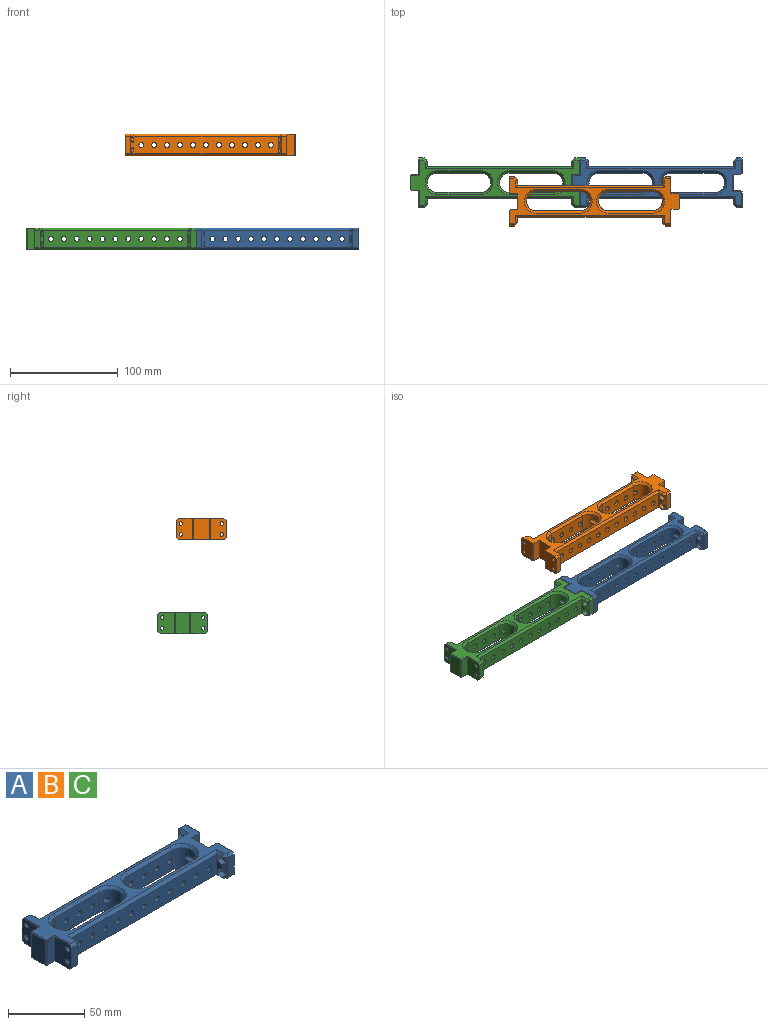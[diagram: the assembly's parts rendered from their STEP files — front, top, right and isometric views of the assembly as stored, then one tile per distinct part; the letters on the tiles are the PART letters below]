
ASSEMBLY  parts=3 mates=1
PART A: 168 faces, bbox 158.1x46.1x20.1 mm
  f0: plane 16x5mm, normal (1,0,0), area 39.9mm2, adj f20,f83,f84,f106,f142,f149
  f1: plane 0.54x0.14mm, normal (1,0,0), area 0mm2, adj f84,f106,f142
  f2: plane 16x5mm, normal (-1,0,0), area 37mm2, adj f20,f66,f67,f68,f69,f73,f74,f75
  f3: plane 0.13x0.08mm, normal (-1,0,0), area 0mm2, adj f77,f109,f151
  f4: plane 16x5mm, normal (-1,0,0), area 37mm2, adj f26,f86,f89,f90,f91,f93,f94,f97
  f5: plane 0.13x0.08mm, normal (-1,0,0), area 0mm2, adj f88,f108,f128
  f6: plane 16x5mm, normal (1,0,0), area 39.9mm2, adj f26,f102,f105,f107,f130,f137
  f7: plane 0.54x0.14mm, normal (1,0,0), area 0mm2, adj f102,f107,f137
  f8: cylinder r=1.7mm len=4mm, axis (-1,0,0), area 42.7mm2, adj f10,f104
  f9: cylinder r=1.7mm len=4mm, axis (-1,0,0), area 42.7mm2, adj f10,f103
  f10: plane 19.5x15.58mm, normal (-1,0,0), area 282.4mm2, adj f8,f9,f24,f25,f33,f132,f139,f161
  f11: plane 0.54x0.14mm, normal (1,0,0), area 0mm2, adj f105,f107,f130
  f12: plane 19.5x14.43mm, normal (1,0,0), area 260mm2, adj f27,f33,f62,f100,f101,f126,f133,f158
  f13: plane 0.13x0.08mm, normal (-1,0,0), area 0mm2, adj f95,f108,f135
  f14: cylinder r=1.7mm len=4mm, axis (-1,0,0), area 42.7mm2, adj f17,f85
  f15: cylinder r=1.7mm len=4mm, axis (-1,0,0), area 42.7mm2, adj f17,f82
  f16: plane 0.54x0.14mm, normal (1,0,0), area 0mm2, adj f83,f106,f149
  f17: plane 19.5x15.58mm, normal (-1,0,0), area 282.4mm2, adj f14,f15,f21,f22,f33,f140,f147,f167
  f18: plane 19.5x14.43mm, normal (1,0,0), area 260mm2, adj f31,f33,f63,f80,f81,f146,f153,f154
  f19: plane 0.13x0.08mm, normal (-1,0,0), area 0mm2, adj f70,f109,f144
  f20: plane 134x16mm, normal (0,1,0), area 1953.2mm2, adj f0,f2,f42,f48,f49,f50,f51,f52
  f21: plane 16x5mm, normal (0,1,0), area 80mm2, adj f17,f106,f140,f147
  f22: plane 19.5x7mm, normal (0,1,0), area 136.5mm2, adj f17,f33,f65,f166
  f23: plane 19.5x12.85mm, normal (-1,0,0), area 250.6mm2, adj f33,f64,f65,f164
  f24: plane 19.5x7mm, normal (0,-1,0), area 136.5mm2, adj f10,f33,f64,f162
  f25: plane 16x5mm, normal (0,-1,0), area 80mm2, adj f10,f107,f132,f139
  f26: plane 134x16mm, normal (0,-1,0), area 1953.2mm2, adj f4,f6,f43,f44,f45,f46,f47,f52
  f27: plane 16x5mm, normal (0,-1,0), area 80mm2, adj f12,f108,f126,f133
  f28: plane 19.5x7mm, normal (0,1,0), area 136.5mm2, adj f29,f33,f62,f159
  f29: plane 19.5x15.15mm, normal (1,0,0), area 295.4mm2, adj f28,f30,f33,f157
  f30: plane 19.5x7mm, normal (0,-1,0), area 136.5mm2, adj f29,f33,f63,f156
  f31: plane 16x5mm, normal (0,1,0), area 80mm2, adj f18,f109,f146,f153
  f32: plane 157x42mm, normal (0,0,1), area 1459.6mm2, adj f118,f119,f120,f121,f122,f123,f124,f125
  f33: plane 158x42mm, normal (0,0,-1), area 1516.6mm2, adj f10,f12,f17,f18,f22,f23,f24,f28
  f34: plane 41x16mm, normal (0,-1,0), area 587.2mm2, adj f35,f37,f54,f59,f60,f61,f110,f118
  f35: cylinder r=9mm len=18mm, axis (0,0,1), area 398.1mm2, adj f34,f36,f58,f111,f119
  f36: plane 41x16mm, normal (0,1,0), area 587.2mm2, adj f35,f37,f53,f55,f56,f57,f113,f121
  f37: cylinder r=9mm len=18mm, axis (0,0,1), area 416.1mm2, adj f34,f36,f52,f53,f54,f112,f120
  f38: plane 41x16mm, normal (0,-1,0), area 603.4mm2, adj f39,f41,f48,f49,f50,f51,f114,f122
  f39: cylinder r=9mm len=18mm, axis (0,0,1), area 417.6mm2, adj f38,f40,f47,f48,f115,f123
  f40: plane 41x16mm, normal (0,1,0), area 603.4mm2, adj f39,f41,f44,f45,f46,f47,f117,f125
  f41: cylinder r=9mm len=18mm, axis (0,0,1), area 409.2mm2, adj f38,f40,f42,f43,f116,f124
  f42: cylinder r=2.35mm len=9.81mm, axis (0,1,0), area 115.2mm2, adj f20,f41
  f43: cylinder r=2.35mm len=9.81mm, axis (0,1,0), area 115.2mm2, adj f26,f41
  f44: cylinder r=2.35mm len=6mm, axis (0,1,0), area 88.6mm2, adj f26,f40
  f45: cylinder r=2.35mm len=6mm, axis (0,1,0), area 88.6mm2, adj f26,f40
  f46: cylinder r=2.35mm len=6mm, axis (0,1,0), area 88.6mm2, adj f26,f40
  f47: cylinder r=2.35mm len=7.12mm, axis (0,1,0), area 94.4mm2, adj f26,f39,f40
  f48: cylinder r=2.35mm len=7.12mm, axis (0,1,0), area 94.4mm2, adj f20,f38,f39
  f49: cylinder r=2.35mm len=6mm, axis (0,1,0), area 88.6mm2, adj f20,f38
  f50: cylinder r=2.35mm len=6mm, axis (0,1,0), area 88.6mm2, adj f20,f38
  f51: cylinder r=2.35mm len=6mm, axis (0,1,0), area 88.6mm2, adj f20,f38
  f52: cylinder r=2.35mm len=30mm, axis (0,1,0), area 403.5mm2, adj f20,f26,f37
  f53: cylinder r=2.35mm len=6mm, axis (0,1,0), area 88.6mm2, adj f26,f36,f37
  f54: cylinder r=2.35mm len=6mm, axis (0,1,0), area 88.6mm2, adj f20,f34,f37
  f55: cylinder r=2.35mm len=6mm, axis (0,1,0), area 88.6mm2, adj f26,f36
  f56: cylinder r=2.35mm len=6mm, axis (0,1,0), area 88.6mm2, adj f26,f36
  f57: cylinder r=2.35mm len=6mm, axis (0,1,0), area 88.6mm2, adj f26,f36
  f58: cylinder r=2.35mm len=30mm, axis (0,1,0), area 373.3mm2, adj f20,f26,f35
  f59: cylinder r=2.35mm len=6mm, axis (0,1,0), area 88.6mm2, adj f20,f34
  f60: cylinder r=2.35mm len=6mm, axis (0,1,0), area 88.6mm2, adj f20,f34
  f61: cylinder r=2.35mm len=6mm, axis (0,1,0), area 88.6mm2, adj f20,f34
  f62: plane 19.5x1mm, normal (0.71,0.71,0), area 27.6mm2, adj f12,f28,f33,f160
  f63: plane 19.5x1mm, normal (0.71,-0.71,0), area 27.6mm2, adj f18,f30,f33,f155
  f64: plane 19.5x1mm, normal (-0.71,-0.71,0), area 27.6mm2, adj f23,f24,f33,f163
  f65: plane 19.5x1mm, normal (-0.71,0.71,0), area 27.6mm2, adj f22,f23,f33,f165
  f66: plane 4x3mm, normal (0,-0.5,0.87), area 11.5mm2, adj f2,f67,f71,f72,f109
  f67: plane 4x3mm, normal (0,0.5,0.87), area 13.9mm2, adj f2,f66,f68,f72
  f68: plane 4x3.46mm, normal (0,1,0), area 13.9mm2, adj f2,f67,f69,f72
  f69: plane 4x3mm, normal (0,0.5,-0.87), area 13.6mm2, adj f2,f68,f70,f72,f144
  f70: plane 4x3mm, normal (0,-0.5,-0.87), area 11.3mm2, adj f19,f69,f71,f72,f109,f144
  f71: plane 3.46x2mm, normal (0,-1,0), area 6.9mm2, adj f66,f70,f72,f109
  f72: plane 6.93x6mm, normal (-1,0,0), area 22.1mm2, adj f66,f67,f68,f69,f70,f71,f81
  f73: plane 4x3.46mm, normal (0,1,0), area 13.9mm2, adj f2,f74,f78,f79
  f74: plane 4x3mm, normal (0,0.5,-0.87), area 13.9mm2, adj f2,f73,f75,f79
  f75: plane 4x3mm, normal (0,-0.5,-0.87), area 11.5mm2, adj f2,f74,f76,f79,f109
  f76: plane 3.46x2mm, normal (0,-1,0), area 6.9mm2, adj f75,f77,f79,f109
  f77: plane 4x3mm, normal (0,-0.5,0.87), area 11.3mm2, adj f3,f76,f78,f79,f109,f151
  f78: plane 4x3mm, normal (0,0.5,0.87), area 13.6mm2, adj f2,f73,f77,f79,f151
  f79: plane 6.93x6mm, normal (-1,0,0), area 22.1mm2, adj f73,f74,f75,f76,f77,f78,f80
  f80: cylinder r=1.7mm len=4mm, axis (-1,0,0), area 42.7mm2, adj f18,f79
  f81: cylinder r=1.7mm len=4mm, axis (-1,0,0), area 42.7mm2, adj f18,f72
  f82: plane 6x6mm, normal (1,0,0), area 19.2mm2, adj f15,f83
  f83: cylinder r=3mm len=6mm, axis (1,0,0), area 65.8mm2, adj f0,f16,f82,f106,f149
  f84: cylinder r=3mm len=6mm, axis (1,0,0), area 65.8mm2, adj f0,f1,f85,f106,f142
  f85: plane 6x6mm, normal (1,0,0), area 19.2mm2, adj f14,f84
  f86: plane 4x3mm, normal (0,0.5,0.87), area 11.5mm2, adj f4,f87,f91,f92,f108
  f87: plane 3.46x2mm, normal (0,1,0), area 6.9mm2, adj f86,f88,f92,f108
  f88: plane 4x3mm, normal (0,0.5,-0.87), area 11.3mm2, adj f5,f87,f89,f92,f108,f128
  f89: plane 4x3mm, normal (0,-0.5,-0.87), area 13.6mm2, adj f4,f88,f90,f92,f128
  f90: plane 4x3.46mm, normal (0,-1,0), area 13.9mm2, adj f4,f89,f91,f92
  f91: plane 4x3mm, normal (0,-0.5,0.87), area 13.9mm2, adj f4,f86,f90,f92
  f92: plane 6.93x6mm, normal (-1,0,0), area 22.1mm2, adj f86,f87,f88,f89,f90,f91,f101
  f93: plane 4x3.46mm, normal (0,-1,0), area 13.9mm2, adj f4,f94,f98,f99
  f94: plane 4x3mm, normal (0,-0.5,0.87), area 13.6mm2, adj f4,f93,f95,f99,f135
  f95: plane 4x3mm, normal (0,0.5,0.87), area 11.3mm2, adj f13,f94,f96,f99,f108,f135
  f96: plane 3.46x2mm, normal (0,1,0), area 6.9mm2, adj f95,f97,f99,f108
  f97: plane 4x3mm, normal (0,0.5,-0.87), area 11.5mm2, adj f4,f96,f98,f99,f108
  f98: plane 4x3mm, normal (0,-0.5,-0.87), area 13.9mm2, adj f4,f93,f97,f99
  f99: plane 6.93x6mm, normal (-1,0,0), area 22.1mm2, adj f93,f94,f95,f96,f97,f98,f100
  f100: cylinder r=1.7mm len=4mm, axis (-1,0,0), area 42.7mm2, adj f12,f99
  f101: cylinder r=1.7mm len=4mm, axis (-1,0,0), area 42.7mm2, adj f12,f92
  f102: cylinder r=3mm len=6mm, axis (1,0,0), area 65.8mm2, adj f6,f7,f103,f107,f137
  f103: plane 6x6mm, normal (1,0,0), area 19.2mm2, adj f9,f102
  f104: plane 6x6mm, normal (1,0,0), area 19.2mm2, adj f8,f105
  f105: cylinder r=3mm len=6mm, axis (1,0,0), area 65.8mm2, adj f6,f11,f104,f107,f130
  f106: plane 16x3mm, normal (0.71,0.71,0), area 44.5mm2, adj f0,f1,f16,f21,f83,f84,f141,f148
  f107: plane 16x3mm, normal (0.71,-0.71,0), area 44.5mm2, adj f6,f7,f11,f25,f102,f105,f131,f138
  f108: plane 16x3mm, normal (-0.71,-0.71,0), area 41.8mm2, adj f4,f5,f13,f27,f86,f87,f88,f95
  f109: plane 16x3mm, normal (-0.71,0.71,0), area 41.8mm2, adj f2,f3,f19,f31,f66,f70,f71,f75
  f110: plane 41x2mm, normal (0,-0.71,-0.71), area 116mm2, adj f33,f34,f111,f112
  f111: cone r=9mm half-angle=45deg, axis (0,0,-1), area 88.9mm2, adj f33,f35,f110,f113
  f112: cone r=9mm half-angle=45deg, axis (0,0,-1), area 88.9mm2, adj f33,f37,f110,f113
  f113: plane 41x2mm, normal (0,0.71,-0.71), area 116mm2, adj f33,f36,f111,f112
  f114: plane 41x2mm, normal (0,-0.71,-0.71), area 116mm2, adj f33,f38,f115,f116
  f115: cone r=9mm half-angle=45deg, axis (0,0,-1), area 88.9mm2, adj f33,f39,f114,f117
  f116: cone r=9mm half-angle=45deg, axis (0,0,-1), area 88.9mm2, adj f33,f41,f114,f117
  f117: plane 41x2mm, normal (0,0.71,-0.71), area 116mm2, adj f33,f40,f115,f116
  f118: plane 41x2mm, normal (0,-0.71,0.71), area 116mm2, adj f32,f34,f119,f120
  f119: cone r=11mm half-angle=45deg, axis (0,0,1), area 88.9mm2, adj f32,f35,f118,f121
  f120: cone r=11mm half-angle=45deg, axis (0,0,1), area 88.9mm2, adj f32,f37,f118,f121
  f121: plane 41x2mm, normal (0,0.71,0.71), area 116mm2, adj f32,f36,f119,f120
  f122: plane 41x2mm, normal (0,-0.71,0.71), area 116mm2, adj f32,f38,f123,f124
  f123: cone r=11mm half-angle=45deg, axis (0,0,1), area 88.9mm2, adj f32,f39,f122,f125
  f124: cone r=11mm half-angle=45deg, axis (0,0,1), area 88.9mm2, adj f32,f41,f122,f125
  f125: plane 41x2mm, normal (0,0.71,0.71), area 116mm2, adj f32,f40,f123,f124
  f126: plane 5x2mm, normal (0,-0.71,0.71), area 12.8mm2, adj f12,f27,f32,f127,f158
  f127: plane 3.83x3.83mm, normal (-0.5,-0.5,0.71), area 9.7mm2, adj f32,f108,f126,f128
  f128: plane 7x2mm, normal (-0.71,0,0.71), area 15.2mm2, adj f4,f5,f32,f88,f89,f127,f129
  f129: plane 138x2mm, normal (0,-0.71,0.71), area 384.7mm2, adj f26,f32,f128,f130
  f130: plane 7.07x2.07mm, normal (0.71,0,0.71), area 15.8mm2, adj f6,f11,f32,f105,f129,f131
  f131: plane 3.83x3.83mm, normal (0.5,-0.5,0.71), area 9.7mm2, adj f32,f107,f130,f132
  f132: plane 5x2mm, normal (0,-0.71,0.71), area 12.8mm2, adj f10,f25,f32,f131,f161
  f133: plane 5x2mm, normal (0,-0.71,-0.71), area 13mm2, adj f12,f27,f33,f134
  f134: plane 3.83x3.83mm, normal (-0.5,-0.5,-0.71), area 9.7mm2, adj f33,f108,f133,f135
  f135: plane 7x2mm, normal (-0.71,0,-0.71), area 15.2mm2, adj f4,f13,f33,f94,f95,f134,f136
  f136: plane 138x2mm, normal (0,-0.71,-0.71), area 384.7mm2, adj f26,f33,f135,f137
  f137: plane 7.02x2.02mm, normal (0.71,0,-0.71), area 15.8mm2, adj f6,f7,f33,f102,f136,f138
  f138: plane 3.83x3.83mm, normal (0.5,-0.5,-0.71), area 9.7mm2, adj f33,f107,f137,f139
  f139: plane 5x2mm, normal (0,-0.71,-0.71), area 13mm2, adj f10,f25,f33,f138
  f140: plane 5x2mm, normal (0,0.71,0.71), area 12.8mm2, adj f17,f21,f32,f141,f167
  f141: plane 3.83x3.83mm, normal (0.5,0.5,0.71), area 9.7mm2, adj f32,f106,f140,f142
  f142: plane 7.07x2.07mm, normal (0.71,0,0.71), area 15.8mm2, adj f0,f1,f32,f84,f141,f143
  f143: plane 138x2mm, normal (0,0.71,0.71), area 384.7mm2, adj f20,f32,f142,f144
  f144: plane 7x2mm, normal (-0.71,0,0.71), area 15.2mm2, adj f2,f19,f32,f69,f70,f143,f145
  f145: plane 3.83x3.83mm, normal (-0.5,0.5,0.71), area 9.7mm2, adj f32,f109,f144,f146
  f146: plane 5x2mm, normal (0,0.71,0.71), area 12.8mm2, adj f18,f31,f32,f145,f154
  f147: plane 5x2mm, normal (0,0.71,-0.71), area 13mm2, adj f17,f21,f33,f148
  f148: plane 3.83x3.83mm, normal (0.5,0.5,-0.71), area 9.7mm2, adj f33,f106,f147,f149
  f149: plane 7.02x2.02mm, normal (0.71,0,-0.71), area 15.8mm2, adj f0,f16,f33,f83,f148,f150
  f150: plane 138x2mm, normal (0,0.71,-0.71), area 384.7mm2, adj f20,f33,f149,f151
  f151: plane 7x2mm, normal (-0.71,0,-0.71), area 15.2mm2, adj f2,f3,f33,f77,f78,f150,f152
  f152: plane 3.83x3.83mm, normal (-0.5,0.5,-0.71), area 9.7mm2, adj f33,f109,f151,f153
  f153: plane 5x2mm, normal (0,0.71,-0.71), area 13mm2, adj f18,f31,f33,f152
  f154: plane 12.93x0.5mm, normal (0.71,0,0.71), area 8.9mm2, adj f18,f32,f146,f155
  f155: plane 1.21x1.21mm, normal (0.5,-0.5,0.71), area 0.9mm2, adj f32,f63,f154,f156
  f156: plane 7.5x0.5mm, normal (0,-0.71,0.71), area 5.1mm2, adj f30,f32,f155,f157
  f157: plane 16.15x0.5mm, normal (0.71,0,0.71), area 11.1mm2, adj f29,f32,f156,f159
  f158: plane 12.93x0.5mm, normal (0.71,0,0.71), area 8.9mm2, adj f12,f32,f126,f160
  f159: plane 7.5x0.5mm, normal (0,0.71,0.71), area 5.1mm2, adj f28,f32,f157,f160
  f160: plane 1.21x1.21mm, normal (0.5,0.5,0.71), area 0.9mm2, adj f32,f62,f158,f159
  f161: plane 14.58x0.5mm, normal (-0.71,0,0.71), area 10mm2, adj f10,f32,f132,f162
  f162: plane 7.5x0.5mm, normal (0,-0.71,0.71), area 5.1mm2, adj f24,f32,f161,f163
  f163: plane 1.21x1.21mm, normal (-0.5,-0.5,0.71), area 0.9mm2, adj f32,f64,f162,f164
  f164: plane 12.85x0.5mm, normal (-0.71,0,0.71), area 8.9mm2, adj f23,f32,f163,f165
  f165: plane 1.21x1.21mm, normal (-0.5,0.5,0.71), area 0.9mm2, adj f32,f65,f164,f166
  f166: plane 7.5x0.5mm, normal (0,0.71,0.71), area 5.1mm2, adj f22,f32,f165,f167
  f167: plane 14.58x0.5mm, normal (-0.71,0,0.71), area 10mm2, adj f17,f32,f140,f166
PART B: same geometry as A
PART C: same geometry as A
PLACE A t=(78.87,-26.55,44.64)mm
PLACE B rot(axis=(0,-1,0),180deg) t=(12.87,-43.9,151.83)mm
PLACE C t=(-71.13,-26.55,44.64)mm
MATE fastened A.f23 <-> C.f29  axis (-1,0,0) through (-4.13,-26.55,54.39)mm
